# Revit family: 506_VCE-A-_-G-ZP-0-0
name_source: partatom
category: Electrical Equipment
revit_build: Autodesk Revit 2018 (Build: 20170223_1515(x64)
units: mm (PartAtom-declared; Revit-internal decimal feet)

## family parameters
Always vertical = Yes
Cut with Voids When Loaded = No
Part Type = Equipment Switch
Room Calculation Point = No
Round Connector Dimension = Use Diameter
Shared = No
Work Plane-Based = No

## types (3) — shared parameters
Description = Air curtain ESSENSSE, output series A, electric heater
H = 169 mm  [stored 0.554462 ft]
MC Active Power = 1 W
MC CosPhi = 0.95
MC Number of Poles = 3
MC Voltage = 0 V
MT1 = No
MT2 = Yes
Manufacturer = 2VV
PHR = 20 mm  [stored 0.0656168 ft]
PHS = 20 mm  [stored 0.0656168 ft]
R1 = 85 mm
URL = www.2vv.cz
W2 = 169 mm  [stored 0.554462 ft]
W3 = 84 mm  [stored 0.275591 ft]
Y1 = 20 mm  [stored 0.0656168 ft]
magiApparentLoad = 1 VA
magiPartTypeId = 506
magiProductFamilyId = VCE-A-*-G-ZP-0-0
zero-valued in all types: L2D, W2D

## per-type parameters (varying)
| type | L | L2 | L3 | L__ve |
| VCE-A-100-G-ZP-0-0 | 1035 mm  [stored 3.39567 ft] | 518 mm | 468 mm | -1035 mm  [stored -3.39567 ft] |
| VCE-A-200-G-ZP-0-0 | 2035 mm | 1018 mm | 968 mm | -2035 mm |
| VCE-A-150-G-ZP-0-0 | 1535 mm | 768 mm | 718 mm | -1535 mm |

note: column(s) folded — value = type name in every type: MC Product Code, magiProductId

note: [stored X ft] marks values corroborated as IEEE doubles in the binary element streams (Revit-internal decimal feet)

## geometry (parser evidence)
native form markers: Blend x2, Sweep x2
no freeform markers — native parametric forms only
